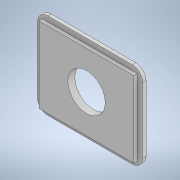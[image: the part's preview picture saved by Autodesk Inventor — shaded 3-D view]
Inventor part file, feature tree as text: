
AUTODESK INVENTOR PART (.ipt)
format: ipt  version: 2020 (Build 240168000, 168)  size: 124,416 bytes
history: native  units: mm
features: extrude x2, sketch x2, fillet x1
ambient origin geometry x8: Origin, YZ Plane, XZ Plane, XY Plane, X Axis, Y Axis, Z Axis, Center Point
bodies: Solid1 (feature_tree)
feature tree (5):
  extrude  "Extrusion1"  Depth=22.0mm
  extrude  "Extrusion2"  Depth=1.0mm TaperAngle=0.0deg
  fillet  "Fillet1"  Radius=1.5mm
  sketch  "Sketch1"  dims[d0=27.5mm d1=22.0mm]
  sketch  "Sketch2"  dims[d2=10.8mm d3=1.0mm d4=0.0mm d5=1.5mm d6=1.5mm d7=1.0mm d8=0.0mm d9=3.0mm]
